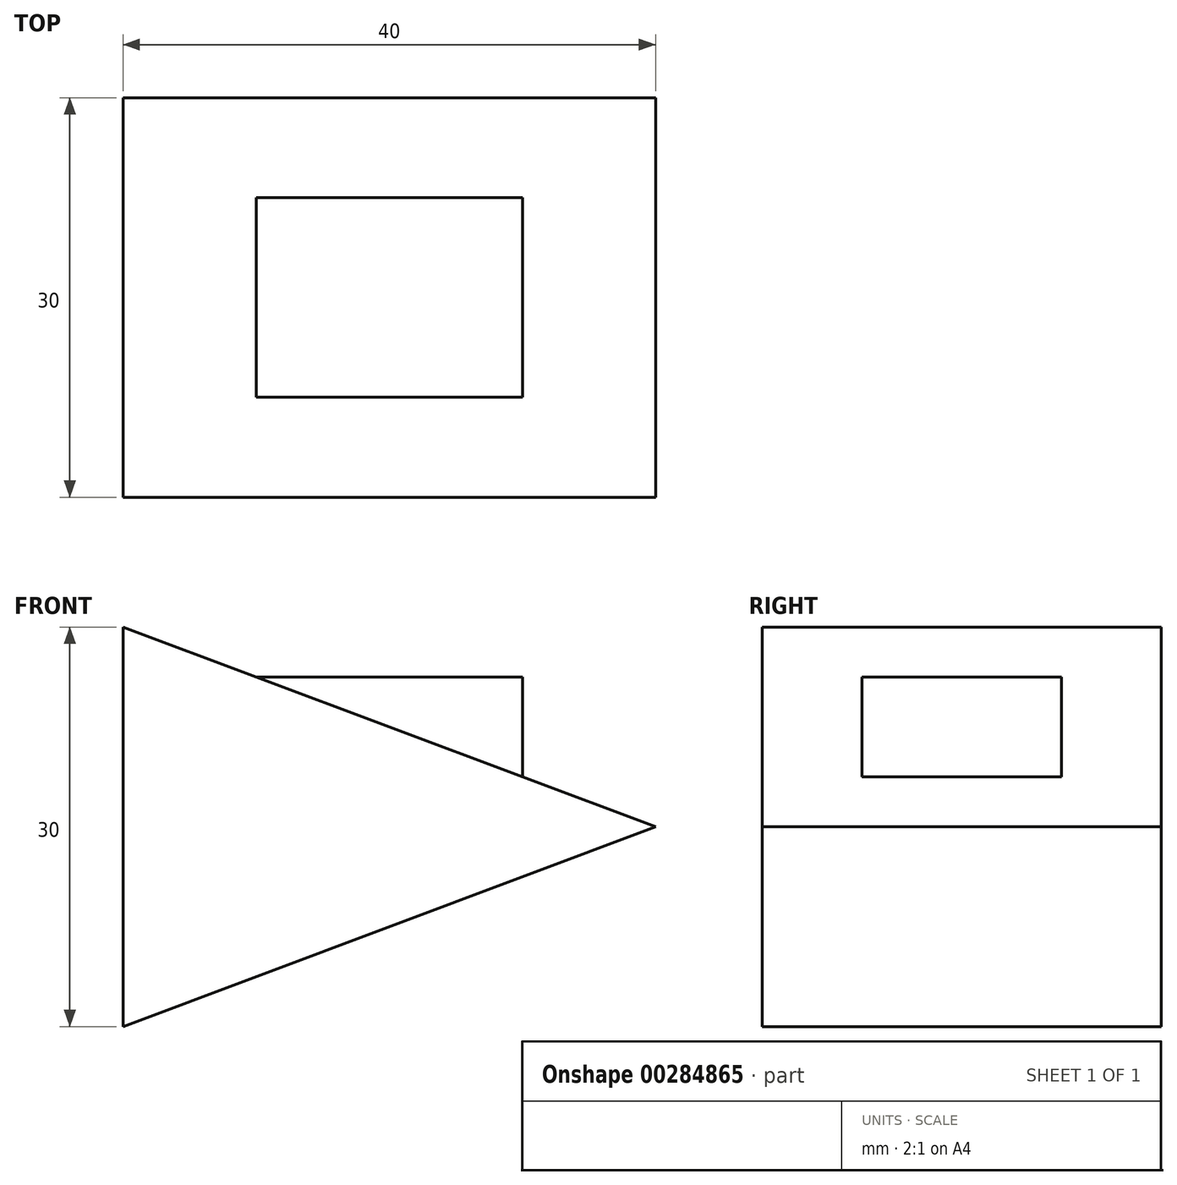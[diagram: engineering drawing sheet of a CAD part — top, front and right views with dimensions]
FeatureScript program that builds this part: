
annotation { "Feature Type Name" : "Feature", "Feature Type Description" : "" }
export const myFeature = defineFeature(function(context is Context, id is Id, definition is map)
    precondition{}
    {
        {
            var Q0;
            Q0=qCreatedBy(makeId("Front.planeOp"),FACE);
            var sketch = newSketch(context, id + "F0", { "sketchPlane" : qUnion([Q0])});
            skLineSegment(sketch, "E0.bottom", {"start": v(0, 0) * mm, "end": v(40, 0) * mm});
            skLineSegment(sketch, "E0.top", {"start": v(0, 30) * mm, "end": v(40, 30) * mm});
            skLineSegment(sketch, "E0.left", {"start": v(0, 0) * mm, "end": v(0, 30) * mm});
            skLineSegment(sketch, "E0.right", {"start": v(40, 0) * mm, "end": v(40, 30) * mm});
            skLineSegment(sketch, "E1", {"start": v(0, 30) * mm, "end": v(40, 15) * mm});
            skLineSegment(sketch, "E2.bottom", {"start": v(10, 26.25) * mm, "end": v(30, 26.25) * mm});
            skLineSegment(sketch, "E2.top", {"start": v(10, 18.75) * mm, "end": v(30, 18.75) * mm});
            skLineSegment(sketch, "E2.left", {"start": v(10, 26.25) * mm, "end": v(10, 18.75) * mm});
            skLineSegment(sketch, "E2.right", {"start": v(30, 26.25) * mm, "end": v(30, 18.75) * mm});
            skLineSegment(sketch, "E3", {"start": v(40, 15) * mm, "end": v(0, 0) * mm});
            skSolve(sketch);
        }
        {
            var Q0;
            {var subQ4=sQuery(id+"F0.wireOp",EDGE,"E0.bottom");Q0=makeQuery(id+"F0.imprint","IMPRINT",FACE,{"disambiguationData":[TD([[makeQuery(id+"F0.imprint","IMPRINT",EDGE,{"derivedFrom":subQ4}),1.0]])]});}
            var Q1;
            {var subQ2=sQuery(id+"F0.wireOp",EDGE,"E2.top");Q1=makeQuery(id+"F0.imprint","IMPRINT",FACE,{"disambiguationData":[TD([[makeQuery(id+"F0.imprint","IMPRINT",EDGE,{"derivedFrom":subQ2}),1.0]])]});}
            var Q2;
            {var subQ2=sQuery(id+"F0.wireOp",EDGE,"E0.left");Q2=makeQuery(id+"F0.imprint","IMPRINT",FACE,{"disambiguationData":[TD([[makeQuery(id+"F0.imprint","IMPRINT",EDGE,{"derivedFrom":subQ2}),-1.0]])]});}
            extrude(context, id + "F1", {"entities" : qUnion([Q0, Q1, Q2]), "depth" : 30 * mm, "symmetric" : true});
        }
        {
            var Q0;
            {var subQ0=sQuery(id+"F0.wireOp",EDGE,"E2.bottom");Q0=makeQuery(id+"F0.imprint","IMPRINT",FACE,{"disambiguationData":[TD([[makeQuery(id+"F0.imprint","IMPRINT",EDGE,{"derivedFrom":subQ0}),-1.0]])]});}
            extrude(context, id + "F2", {"entities" : qUnion([Q0]), "operationType" : NewBodyOperationType.ADD, "oppositeDirection" : true, "depth" : 15 * mm, "symmetric" : true});
        }
        {
            var Q0;
            {var subQ0=sQuery(id+"F0.wireOp",EDGE,"E0.bottom");Q0=makeQuery(id+"F0.imprint","IMPRINT",FACE,{"disambiguationData":[TD([[makeQuery(id+"F0.imprint","IMPRINT",EDGE,{"derivedFrom":subQ0}),1.0]])]});}
            extrude(context, id + "F3", {"entities" : qUnion([Q0]), "operationType" : NewBodyOperationType.REMOVE, "oppositeDirection" : true, "depth" : 30 * mm, "symmetric" : true});
        }
    });
